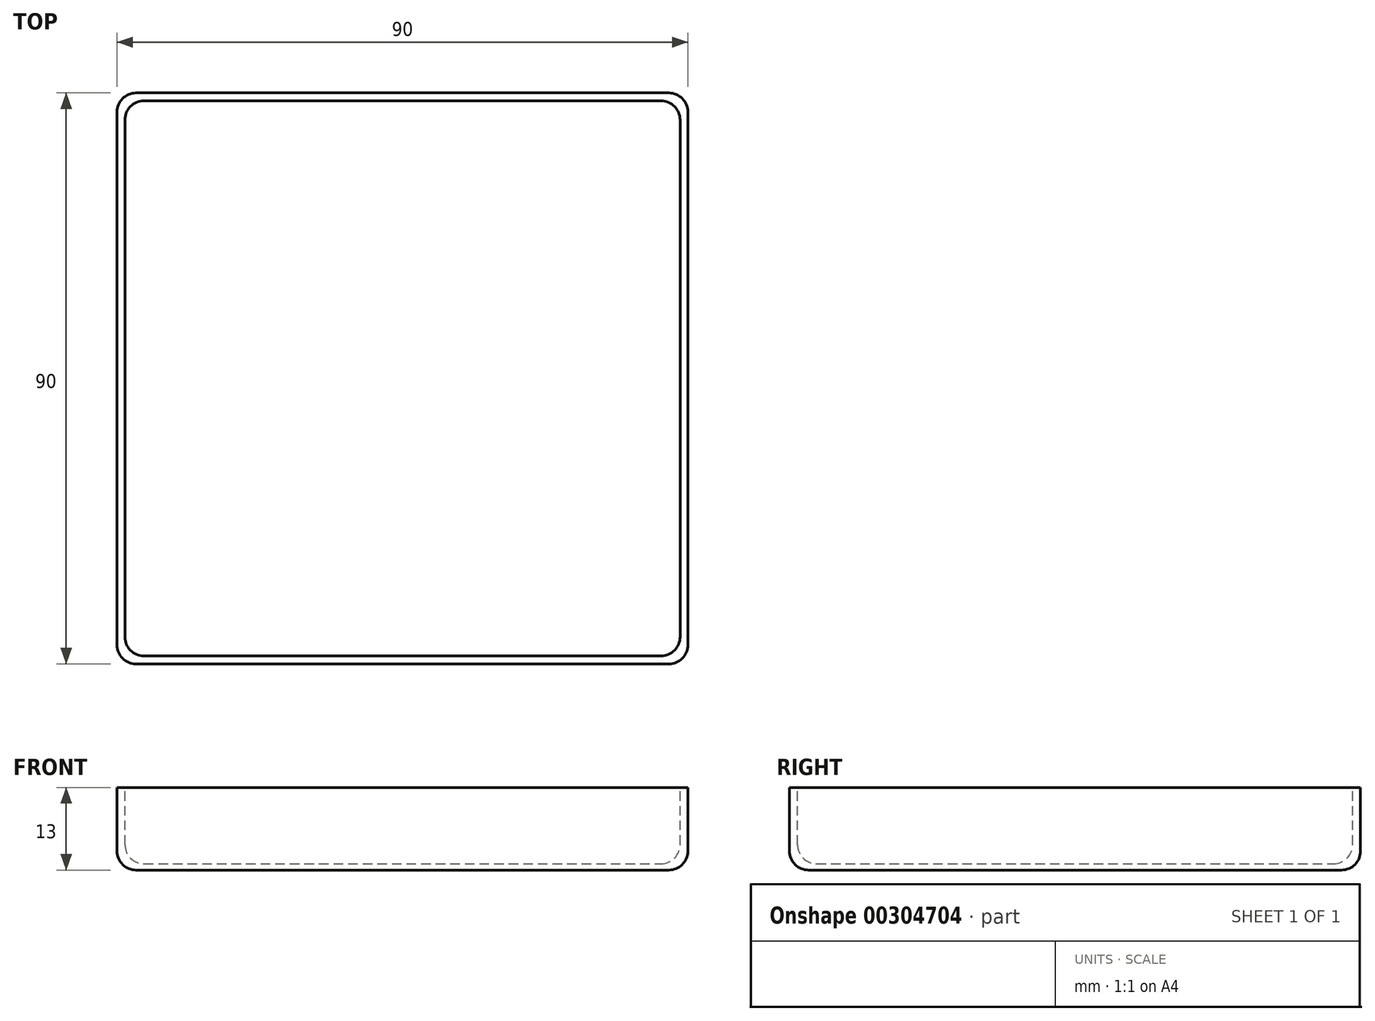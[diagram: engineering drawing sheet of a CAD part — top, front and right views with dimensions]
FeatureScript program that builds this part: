
annotation { "Feature Type Name" : "Feature", "Feature Type Description" : "" }
export const myFeature = defineFeature(function(context is Context, id is Id, definition is map)
    precondition{}
    {
        {
            var Q0;
            Q0=qCreatedBy(makeId("Top.planeOp"),FACE);
            var sketch = newSketch(context, id + "F0", { "sketchPlane" : qUnion([Q0])});
            skLineSegment(sketch, "E0.bottom", {"start": v(45, 45) * mm, "end": v(-45, 45) * mm});
            skLineSegment(sketch, "E0.top", {"start": v(45, -45) * mm, "end": v(-45, -45) * mm});
            skLineSegment(sketch, "E0.left", {"start": v(45, 45) * mm, "end": v(45, -45) * mm});
            skLineSegment(sketch, "E0.right", {"start": v(-45, 45) * mm, "end": v(-45, -45) * mm});
            skPoint(sketch, "E0.middle", {"position": v(0, 0) * mm});
            skSolve(sketch);
        }
        {
            var Q0;
            Q0 = qSketchRegion(id + "F0", true);
            extrude(context, id + "F1", {"entities" : qUnion([Q0]), "depth" : 13 * mm});
        }
        {
            var Q0;
            Q0=makeQuery(id+"F1.opExtrude","CAP_FACE",FACE,{"disambiguationData":[OSD([sQuery(id+"F0.wireOp",EDGE,"E0.bottom"),sQuery(id+"F0.wireOp",EDGE,"E0.top"),sQuery(id+"F0.wireOp",EDGE,"E0.left"),sQuery(id+"F0.wireOp",EDGE,"E0.right")])],"isStart":false});
            var sketch = newSketch(context, id + "F2", { "sketchPlane" : qUnion([Q0])});
            skLineSegment(sketch, "E1.0", {"start": v(-43.75, -43.75) * mm, "end": v(43.75, -43.75) * mm});
            skLineSegment(sketch, "E1.1", {"start": v(-43.75, 43.75) * mm, "end": v(-43.75, -43.75) * mm});
            skLineSegment(sketch, "E1.2", {"start": v(43.75, 43.75) * mm, "end": v(-43.75, 43.75) * mm});
            skLineSegment(sketch, "E1.3", {"start": v(43.75, -43.75) * mm, "end": v(43.75, 43.75) * mm});
            skSolve(sketch);
        }
        {
            var Q0;
            Q0 = qSketchRegion(id + "F2", true);
            extrude(context, id + "F3", {"entities" : qUnion([Q0]), "operationType" : NewBodyOperationType.REMOVE, "oppositeDirection" : true, "depth" : 12 * mm});
        }
        {
            var Q0;
            Q0=makeQuery(id+"F1.opExtrude","CAP_FACE",FACE,{"disambiguationData":[OSD([sQuery(id+"F0.wireOp",EDGE,"E0.bottom"),sQuery(id+"F0.wireOp",EDGE,"E0.top"),sQuery(id+"F0.wireOp",EDGE,"E0.left"),sQuery(id+"F0.wireOp",EDGE,"E0.right")])],"isStart":true});
            var Q1;
            Q1=makeQuery(id+"F1.opExtrude","SWEPT_EDGE",EDGE,{"disambiguationData":[OSD([sQuery(id+"F0.wireOp",EDGE,"E0.top"),sQuery(id+"F0.wireOp",EDGE,"E0.left")])]});
            var Q2;
            Q2=makeQuery(id+"F1.opExtrude","SWEPT_EDGE",EDGE,{"disambiguationData":[OSD([sQuery(id+"F0.wireOp",EDGE,"E0.bottom"),sQuery(id+"F0.wireOp",EDGE,"E0.left")])]});
            var Q3;
            Q3=makeQuery(id+"F1.opExtrude","SWEPT_EDGE",EDGE,{"disambiguationData":[OSD([sQuery(id+"F0.wireOp",EDGE,"E0.top"),sQuery(id+"F0.wireOp",EDGE,"E0.right")])]});
            var Q4;
            Q4=makeQuery(id+"F1.opExtrude","SWEPT_EDGE",EDGE,{"disambiguationData":[OSD([sQuery(id+"F0.wireOp",EDGE,"E0.bottom"),sQuery(id+"F0.wireOp",EDGE,"E0.right")])]});
            var Q5;
            Q5=makeQuery(id+"F3.boolean.opBoolean","COPY",FACE,{"derivedFrom":makeQuery(id+"F3.opExtrude","CAP_FACE",FACE,{"disambiguationData":[OSD([sQuery(id+"F2.wireOp",EDGE,"E1.0"),sQuery(id+"F2.wireOp",EDGE,"E1.1"),sQuery(id+"F2.wireOp",EDGE,"E1.2"),sQuery(id+"F2.wireOp",EDGE,"E1.3")])],"isStart":false})});
            var Q6;
            Q6=makeQuery(id+"F3.boolean.opBoolean","COPY",EDGE,{"derivedFrom":makeQuery(id+"F3.opExtrude","SWEPT_EDGE",EDGE,{"disambiguationData":[OSD([sQuery(id+"F2.wireOp",EDGE,"E1.1"),sQuery(id+"F2.wireOp",EDGE,"E1.2")])]})});
            var Q7;
            Q7=makeQuery(id+"F3.boolean.opBoolean","COPY",EDGE,{"derivedFrom":makeQuery(id+"F3.opExtrude","SWEPT_EDGE",EDGE,{"disambiguationData":[OSD([sQuery(id+"F2.wireOp",EDGE,"E1.2"),sQuery(id+"F2.wireOp",EDGE,"E1.3")])]})});
            var Q8;
            Q8=makeQuery(id+"F3.boolean.opBoolean","COPY",EDGE,{"derivedFrom":makeQuery(id+"F3.opExtrude","SWEPT_EDGE",EDGE,{"disambiguationData":[OSD([sQuery(id+"F2.wireOp",EDGE,"E1.0"),sQuery(id+"F2.wireOp",EDGE,"E1.3")])]})});
            var Q9;
            Q9=makeQuery(id+"F3.boolean.opBoolean","COPY",EDGE,{"derivedFrom":makeQuery(id+"F3.opExtrude","SWEPT_EDGE",EDGE,{"disambiguationData":[OSD([sQuery(id+"F2.wireOp",EDGE,"E1.0"),sQuery(id+"F2.wireOp",EDGE,"E1.1")])]})});
            fillet(context, id + "F4", {"entities" : qUnion([Q0, Q1, Q2, Q3, Q4, Q5, Q6, Q7, Q8, Q9]), "radius" : 3 * mm, "tangentPropagation" : true, "allowEdgeOverflow" : false});
        }
    });
